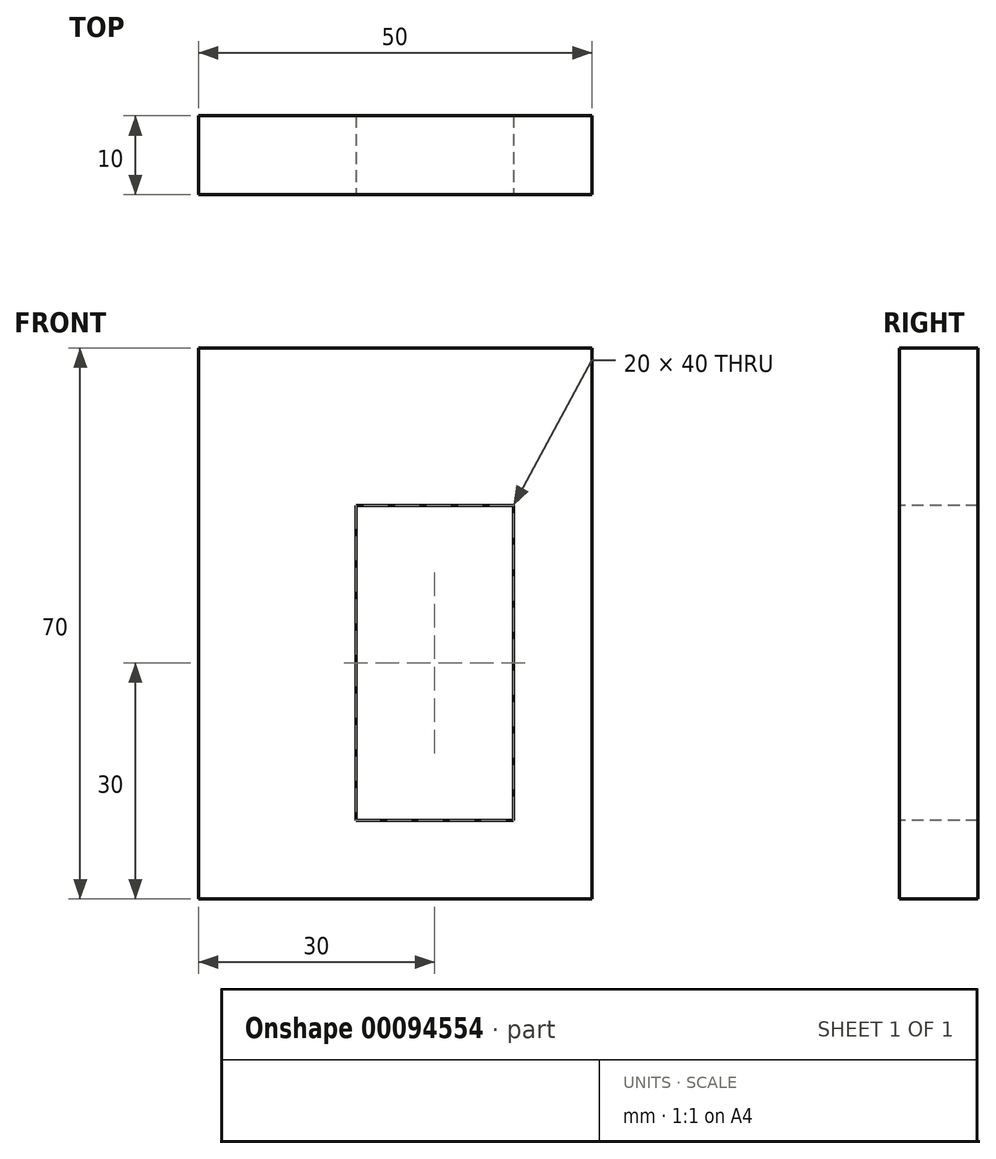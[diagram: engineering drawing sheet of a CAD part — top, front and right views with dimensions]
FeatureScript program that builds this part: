
annotation { "Feature Type Name" : "Feature", "Feature Type Description" : "" }
export const myFeature = defineFeature(function(context is Context, id is Id, definition is map)
    precondition{}
    {
        {
            var Q0;
            Q0=qCreatedBy(makeId("Front.planeOp"),FACE);
            var sketch = newSketch(context, id + "F0", { "sketchPlane" : qUnion([Q0])});
            skLineSegment(sketch, "E0", {"start": v(0, 0) * mm, "end": v(50, 0) * mm});
            skLineSegment(sketch, "E1", {"start": v(50, 0) * mm, "end": v(50, 70) * mm});
            skLineSegment(sketch, "E2", {"start": v(50, 70) * mm, "end": v(0, 70) * mm});
            skLineSegment(sketch, "E3", {"start": v(0, 70) * mm, "end": v(0, 0) * mm});
            skLineSegment(sketch, "E4.bottom", {"start": v(40, 50) * mm, "end": v(20, 50) * mm});
            skLineSegment(sketch, "E4.top", {"start": v(40, 10) * mm, "end": v(20, 10) * mm});
            skLineSegment(sketch, "E4.left", {"start": v(40, 50) * mm, "end": v(40, 10) * mm});
            skLineSegment(sketch, "E4.right", {"start": v(20, 50) * mm, "end": v(20, 10) * mm});
            skSolve(sketch);
        }
        {
            var Q0;
            Q0=makeQuery(id+"F0.imprint","IMPRINT",FACE,{"disambiguationData":[TD([[makeQuery(id+"F0.imprint","IMPRINT",EDGE,{"derivedFrom":sQuery(id+"F0.wireOp",EDGE,"E0")}),1.0]])]});
            extrude(context, id + "F1", {"entities" : qUnion([Q0]), "oppositeDirection" : true, "depth" : 10 * mm});
        }
    });
